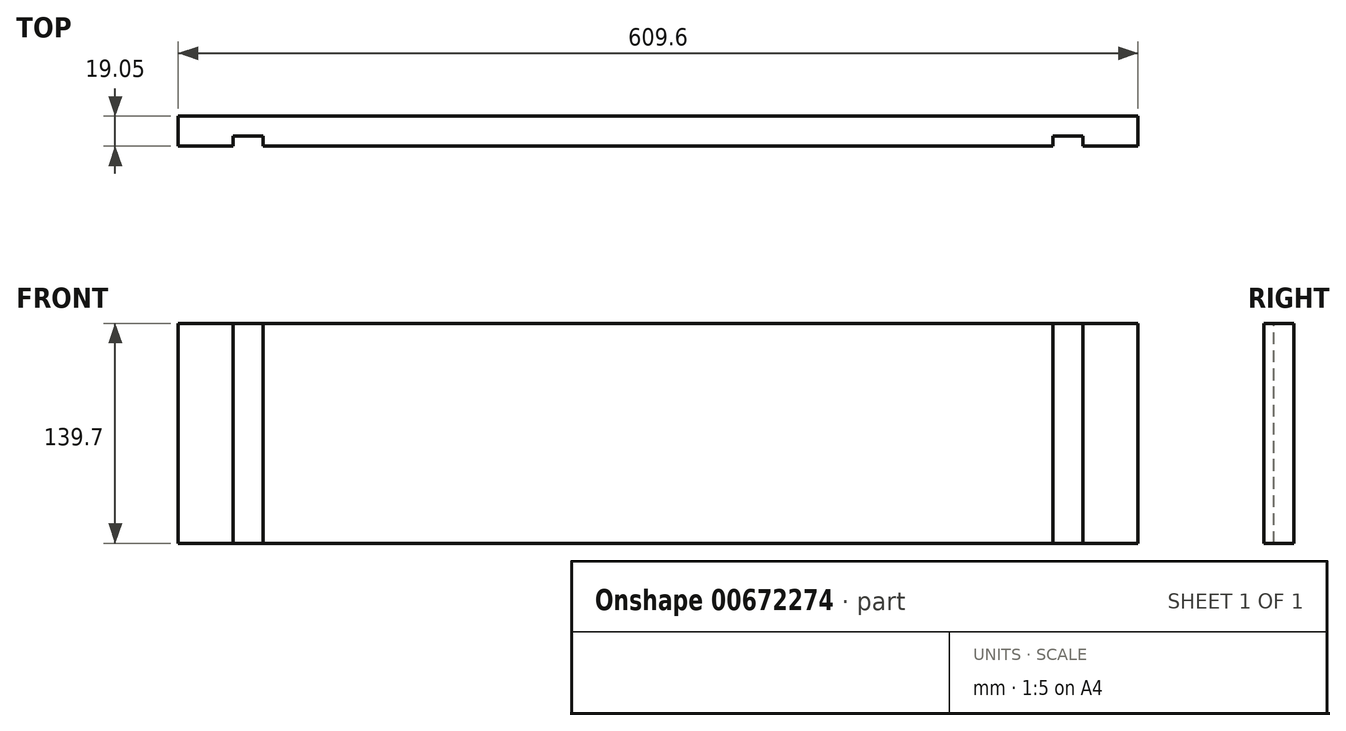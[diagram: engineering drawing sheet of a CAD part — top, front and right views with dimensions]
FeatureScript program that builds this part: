
annotation { "Feature Type Name" : "Feature", "Feature Type Description" : "" }
export const myFeature = defineFeature(function(context is Context, id is Id, definition is map)
    precondition{}
    {
        {
            var Q0;
            Q0=qCreatedBy(makeId("Front.planeOp"),FACE);
            var sketch = newSketch(context, id + "F0", { "sketchPlane" : qUnion([Q0])});
            skLineSegment(sketch, "E0.bottom", {"start": v(0, 139.7) * mm, "end": v(609.6, 139.7) * mm});
            skLineSegment(sketch, "E0.top", {"start": v(0, 0) * mm, "end": v(609.6, 0) * mm});
            skLineSegment(sketch, "E0.left", {"start": v(0, 139.7) * mm, "end": v(0, 0) * mm});
            skLineSegment(sketch, "E0.right", {"start": v(609.6, 139.7) * mm, "end": v(609.6, 0) * mm});
            skSolve(sketch);
        }
        {
            var Q0;
            Q0=makeQuery(id+"F0.imprint","IMPRINT",FACE,{"disambiguationData":[TD([[makeQuery(id+"F0.imprint","IMPRINT",EDGE,{"derivedFrom":sQuery(id+"F0.wireOp",EDGE,"E0.bottom")}),-1.0]])]});
            extrude(context, id + "F1", {"entities" : qUnion([Q0]), "depth" : 19.05 * mm, "offsetDistance" : 25.4 * mm});
        }
        {
            var Q0;
            Q0=makeQuery(id+"F1.opExtrude","SWEPT_FACE",FACE,{"disambiguationData":[OSD([sQuery(id+"F0.wireOp",EDGE,"E0.bottom")])]});
            var sketch = newSketch(context, id + "F2", { "sketchPlane" : qUnion([Q0])});
            skLineSegment(sketch, "E1.bottom", {"start": v(34.92, -19.05) * mm, "end": v(53.97, -19.05) * mm});
            skLineSegment(sketch, "E1.top", {"start": v(34.92, -12.7) * mm, "end": v(53.97, -12.7) * mm});
            skLineSegment(sketch, "E1.left", {"start": v(34.92, -19.05) * mm, "end": v(34.92, -12.7) * mm});
            skLineSegment(sketch, "E1.right", {"start": v(53.97, -19.05) * mm, "end": v(53.97, -12.7) * mm});
            skPoint(sketch, "E2.oppositeSnap0", {"position": v(44.45, -12.7) * mm});
            skLineSegment(sketch, "E2.bottom", {"start": v(574.68, -19.05) * mm, "end": v(555.62, -19.05) * mm});
            skLineSegment(sketch, "E2.top", {"start": v(574.68, -12.7) * mm, "end": v(555.62, -12.7) * mm});
            skLineSegment(sketch, "E2.left", {"start": v(574.68, -19.05) * mm, "end": v(574.68, -12.7) * mm});
            skLineSegment(sketch, "E2.right", {"start": v(555.62, -19.05) * mm, "end": v(555.62, -12.7) * mm});
            skSolve(sketch);
        }
        {
            var Q0;
            Q0 = qSketchRegion(id + "F2", true);
            extrude(context, id + "F3", {"entities" : qUnion([Q0]), "operationType" : NewBodyOperationType.REMOVE, "endBound" : BoundingType.THROUGH_ALL, "oppositeDirection" : true, "depth" : 25.4 * mm, "offsetDistance" : 25.4 * mm});
        }
    });
